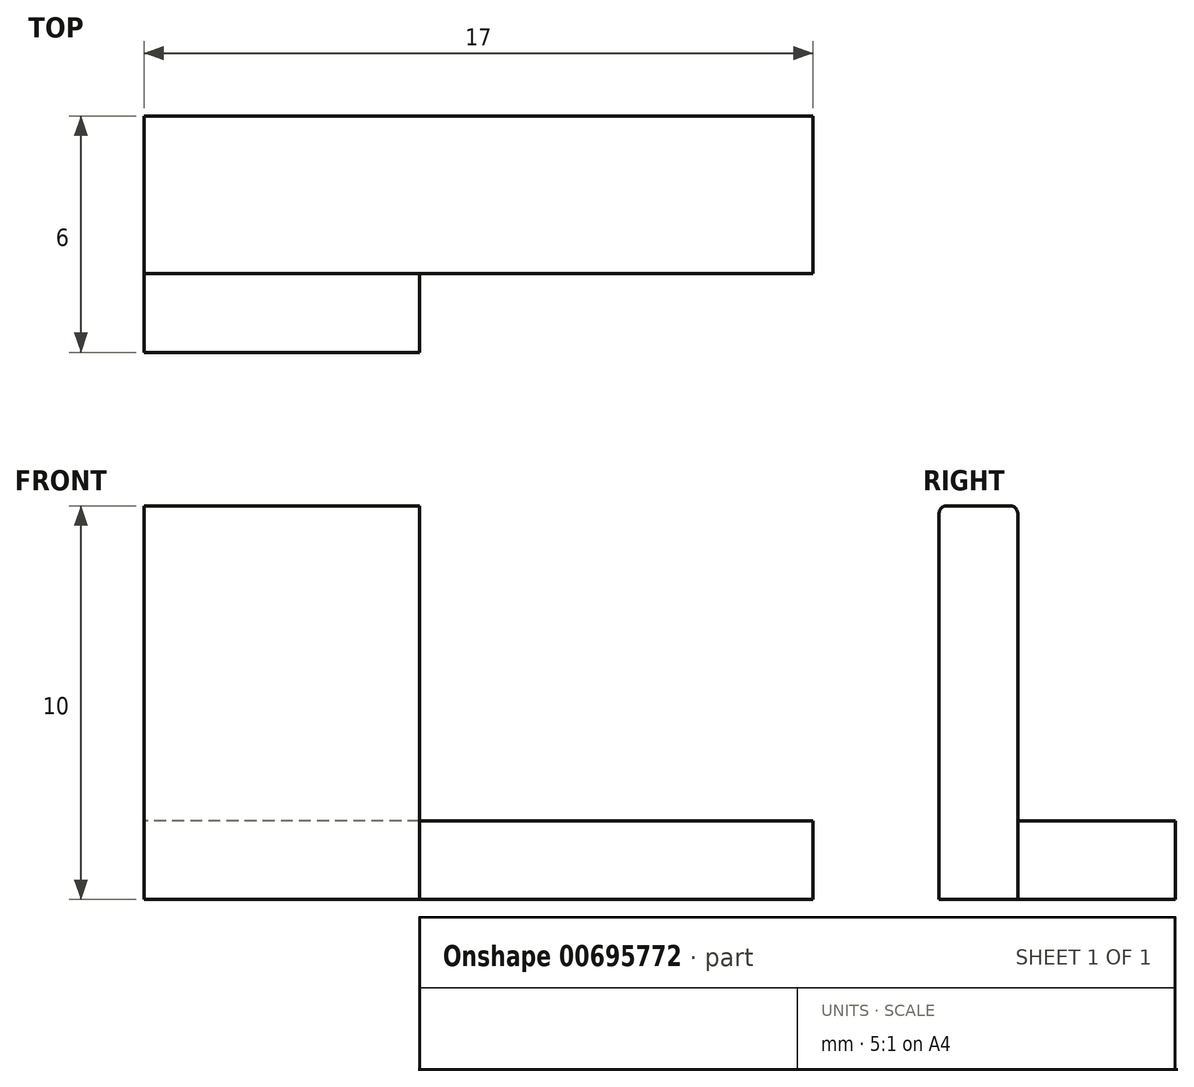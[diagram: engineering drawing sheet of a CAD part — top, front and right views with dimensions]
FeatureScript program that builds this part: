
annotation { "Feature Type Name" : "Feature", "Feature Type Description" : "" }
export const myFeature = defineFeature(function(context is Context, id is Id, definition is map)
    precondition{}
    {
        {
            var Q0;
            Q0=qCreatedBy(makeId("Top.planeOp"),FACE);
            var sketch = newSketch(context, id + "F0", { "sketchPlane" : qUnion([Q0])});
            skLineSegment(sketch, "E0", {"start": v(0, 0) * mm, "end": v(-17, 0) * mm});
            skLineSegment(sketch, "E1", {"start": v(0, 0) * mm, "end": v(0, 4) * mm});
            skLineSegment(sketch, "E2", {"start": v(0, 4) * mm, "end": v(-17, 4) * mm});
            skLineSegment(sketch, "E3", {"start": v(-17, 4) * mm, "end": v(-17, 0) * mm});
            skSolve(sketch);
        }
        {
            var Q0;
            Q0=makeQuery(id+"F0.imprint","IMPRINT",FACE,{"disambiguationData":[TD([[makeQuery(id+"F0.imprint","IMPRINT",EDGE,{"derivedFrom":sQuery(id+"F0.wireOp",EDGE,"E0")}),-1.0]])]});
            extrude(context, id + "F1", {"entities" : qUnion([Q0]), "depth" : 2 * mm});
        }
        {
            var Q0;
            Q0=makeQuery(id+"F1.opExtrude","CAP_FACE",FACE,{"disambiguationData":[OSD([sQuery(id+"F0.wireOp",EDGE,"E0"),sQuery(id+"F0.wireOp",EDGE,"E1"),sQuery(id+"F0.wireOp",EDGE,"E2"),sQuery(id+"F0.wireOp",EDGE,"E3")])],"isStart":true});
            var sketch = newSketch(context, id + "F2", { "sketchPlane" : qUnion([Q0])});
            skLineSegment(sketch, "E4.0.0", {"start": v(-17, 0) * mm, "end": v(0, 0) * mm});
            skLineSegment(sketch, "E4.0.1", {"start": v(0, 0) * mm, "end": v(0, -4) * mm});
            skLineSegment(sketch, "E4.0.2", {"start": v(0, -4) * mm, "end": v(-17, -4) * mm});
            skLineSegment(sketch, "E4.0.3", {"start": v(-17, -4) * mm, "end": v(-17, 0) * mm});
            skLineSegment(sketch, "E5.bottom", {"start": v(-17, -4) * mm, "end": v(0, -4) * mm});
            skLineSegment(sketch, "E5.top", {"start": v(-17, -6) * mm, "end": v(0, -6) * mm});
            skLineSegment(sketch, "E5.left", {"start": v(-17, -4) * mm, "end": v(-17, -6) * mm});
            skLineSegment(sketch, "E5.right", {"start": v(0, -4) * mm, "end": v(0, -6) * mm});
            skLineSegment(sketch, "E6", {"start": v(-10, 0) * mm, "end": v(-10, 2) * mm});
            skLineSegment(sketch, "E7", {"start": v(-10, 2) * mm, "end": v(-17, 2) * mm});
            skLineSegment(sketch, "E8", {"start": v(-17, 2) * mm, "end": v(-17, 0) * mm});
            skSolve(sketch);
        }
        {
            var Q0;
            Q0=makeQuery(id+"F2.imprint","IMPRINT",FACE,{"disambiguationData":[TD([[makeQuery(id+"F2.imprint","IMPRINT",EDGE,{"derivedFrom":sQuery(id+"F2.wireOp",EDGE,"E5.bottom")}),1.0]])]});
            var Q1;
            {var subQ2=sQuery(id+"F2.wireOp",EDGE,"E6");Q1=makeQuery(id+"F2.imprint","IMPRINT",FACE,{"disambiguationData":[TD([[makeQuery(id+"F2.imprint","IMPRINT",EDGE,{"derivedFrom":subQ2}),1.0]])]});}
            extrude(context, id + "F3", {"entities" : qUnion([Q0, Q1]), "operationType" : NewBodyOperationType.ADD, "oppositeDirection" : true, "depth" : 10 * mm});
        }
        {
            var Q0;
            Q0=makeQuery(id+"F3.opExtrude","CAP_EDGE",EDGE,{"disambiguationData":[OSD([sQuery(id+"F2.wireOp",EDGE,"E7")])],"isStart":false});
            var Q1;
            Q1=makeQuery(id+"F3.opExtrude","CAP_EDGE",EDGE,{"disambiguationData":[OSD([sQuery(id+"F2.wireOp",EDGE,"E4.0.0")])],"isStart":false});
            var Q2;
            Q2=makeQuery(id+"F3.opExtrude","CAP_EDGE",EDGE,{"disambiguationData":[OSD([sQuery(id+"F2.wireOp",EDGE,"E5.bottom")])],"isStart":false});
            var Q3;
            Q3=makeQuery(id+"F3.opExtrude","CAP_EDGE",EDGE,{"disambiguationData":[OSD([sQuery(id+"F2.wireOp",EDGE,"E5.top")])],"isStart":false});
            fillet(context, id + "F4", {"entities" : qUnion([Q0, Q1, Q2, Q3]), "radius" : .2 * mm, "tangentPropagation" : true, "allowEdgeOverflow" : false});
        }
    });
